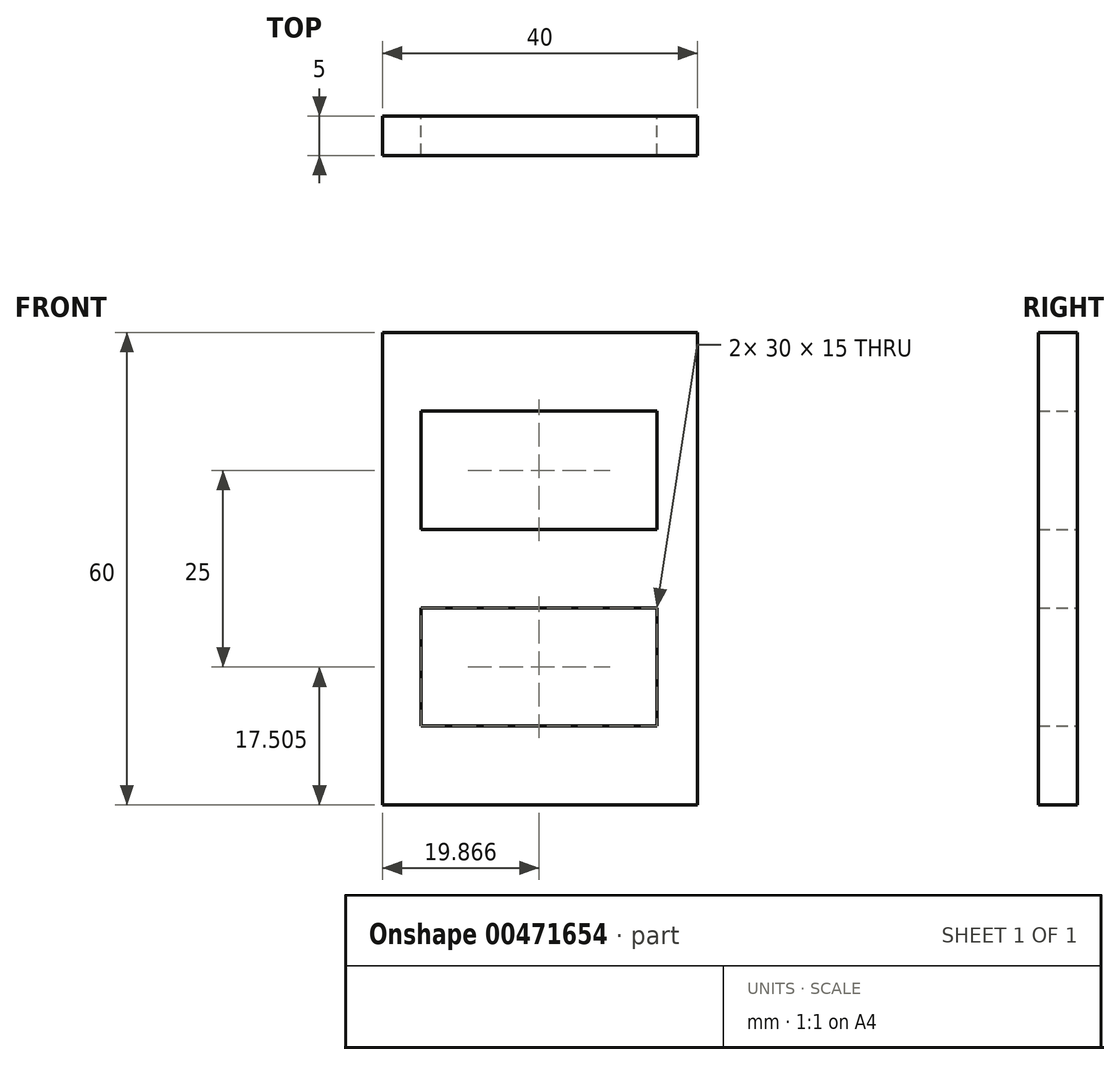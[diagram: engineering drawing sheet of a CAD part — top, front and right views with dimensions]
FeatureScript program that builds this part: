
annotation { "Feature Type Name" : "Feature", "Feature Type Description" : "" }
export const myFeature = defineFeature(function(context is Context, id is Id, definition is map)
    precondition{}
    {
        {
            var Q0;
            Q0=qCreatedBy(makeId("Front.planeOp"),FACE);
            var sketch = newSketch(context, id + "F0", { "sketchPlane" : qUnion([Q0])});
            skLineSegment(sketch, "E0.bottom", {"start": v(-23.63, 29.88) * mm, "end": v(16.37, 29.88) * mm});
            skLineSegment(sketch, "E0.top", {"start": v(-23.63, -30.12) * mm, "end": v(16.37, -30.12) * mm});
            skLineSegment(sketch, "E0.left", {"start": v(-23.63, 29.88) * mm, "end": v(-23.63, -30.12) * mm});
            skLineSegment(sketch, "E0.right", {"start": v(16.37, 29.88) * mm, "end": v(16.37, -30.12) * mm});
            skLineSegment(sketch, "E1.bottom", {"start": v(-18.76, 19.88) * mm, "end": v(11.24, 19.88) * mm});
            skLineSegment(sketch, "E1.top", {"start": v(-18.76, 4.88) * mm, "end": v(11.24, 4.88) * mm});
            skLineSegment(sketch, "E1.left", {"start": v(-18.76, 19.88) * mm, "end": v(-18.76, 4.88) * mm});
            skLineSegment(sketch, "E1.right", {"start": v(11.24, 19.88) * mm, "end": v(11.24, 4.88) * mm});
            skLineSegment(sketch, "E2.bottom", {"start": v(-18.76, -5.12) * mm, "end": v(11.24, -5.12) * mm});
            skLineSegment(sketch, "E2.top", {"start": v(-18.76, -20.12) * mm, "end": v(11.24, -20.12) * mm});
            skLineSegment(sketch, "E2.left", {"start": v(-18.76, -5.12) * mm, "end": v(-18.76, -20.12) * mm});
            skLineSegment(sketch, "E2.right", {"start": v(11.24, -5.12) * mm, "end": v(11.24, -20.12) * mm});
            skSolve(sketch);
        }
        {
            var Q0;
            Q0 = qSketchRegion(id + "F0", true);
            extrude(context, id + "F1", {"entities" : qUnion([Q0]), "depth" : 5 * mm});
        }
    });
